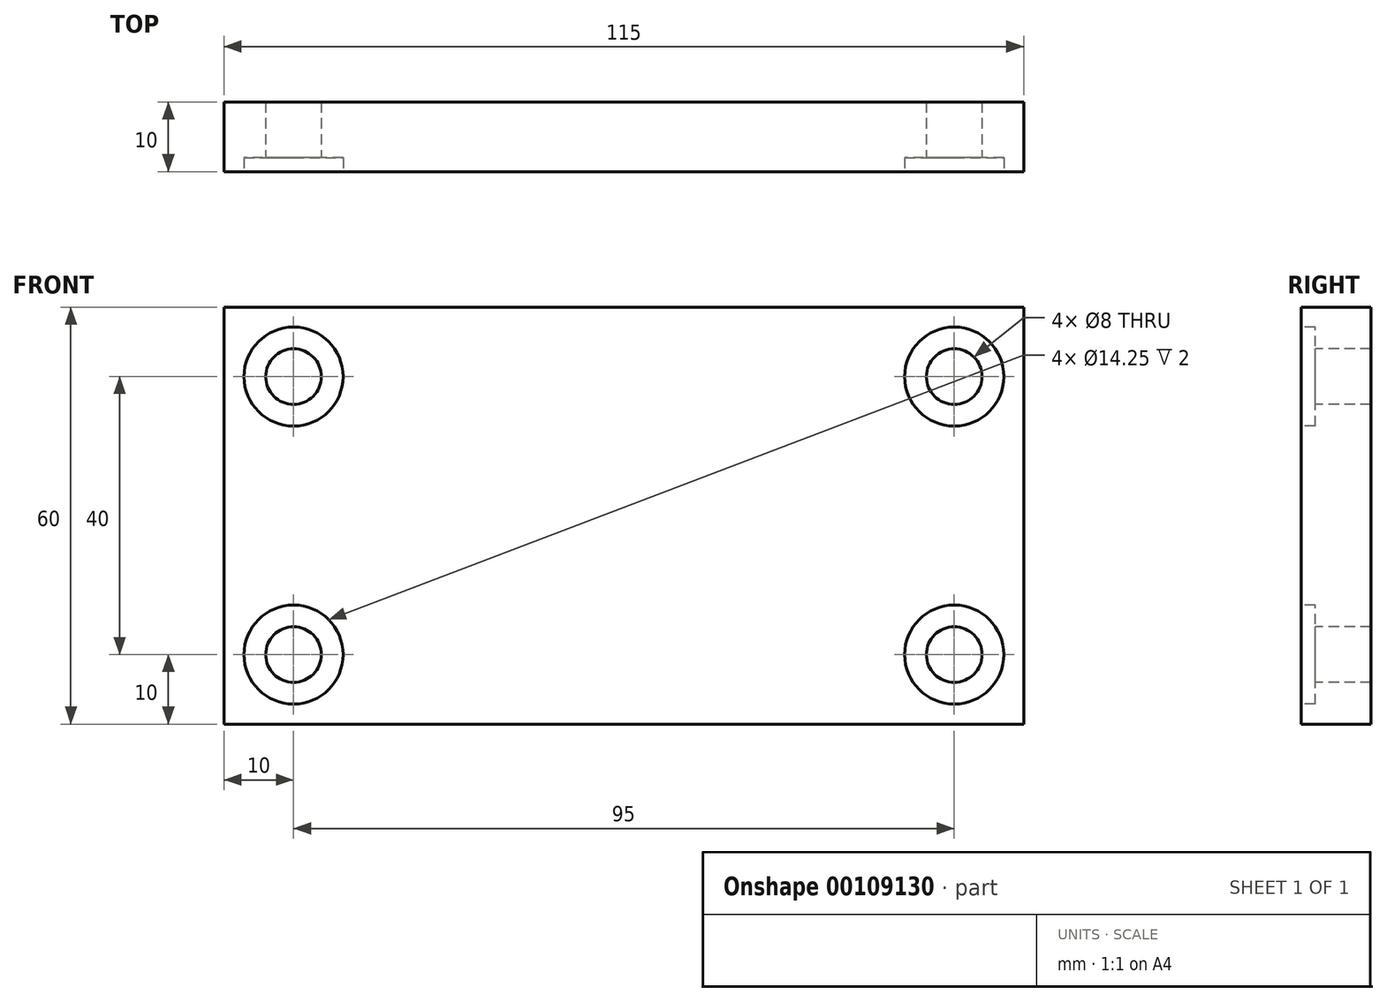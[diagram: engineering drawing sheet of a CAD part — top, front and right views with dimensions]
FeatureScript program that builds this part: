
annotation { "Feature Type Name" : "Feature", "Feature Type Description" : "" }
export const myFeature = defineFeature(function(context is Context, id is Id, definition is map)
    precondition{}
    {
        {
            var Q0;
            Q0=qCreatedBy(makeId("Front.planeOp"),FACE);
            var sketch = newSketch(context, id + "F0", { "sketchPlane" : qUnion([Q0])});
            skLineSegment(sketch, "E0.bottom", {"start": v(0, 0) * mm, "end": v(115, 0) * mm});
            skLineSegment(sketch, "E0.top", {"start": v(0, 60) * mm, "end": v(115, 60) * mm});
            skLineSegment(sketch, "E0.left", {"start": v(0, 0) * mm, "end": v(0, 60) * mm});
            skLineSegment(sketch, "E0.right", {"start": v(115, 0) * mm, "end": v(115, 60) * mm});
            skSolve(sketch);
        }
        {
            var Q0;
            Q0=makeQuery(id+"F0.imprint","IMPRINT",FACE,{"disambiguationData":[TD([[makeQuery(id+"F0.imprint","IMPRINT",EDGE,{"derivedFrom":sQuery(id+"F0.wireOp",EDGE,"E0.bottom")}),1.0]])]});
            extrude(context, id + "F1", {"entities" : qUnion([Q0]), "depth" : 10 * mm});
        }
        {
            var Q0;
            Q0=makeQuery(id+"F1.opExtrude","CAP_FACE",FACE,{"disambiguationData":[OSD([sQuery(id+"F0.wireOp",EDGE,"E0.bottom"),sQuery(id+"F0.wireOp",EDGE,"E0.top"),sQuery(id+"F0.wireOp",EDGE,"E0.left"),sQuery(id+"F0.wireOp",EDGE,"E0.right")])],"isStart":false});
            var sketch = newSketch(context, id + "F2", { "sketchPlane" : qUnion([Q0])});
            skLineSegment(sketch, "E1.bottom", {"start": v(0, 0) * mm, "end": v(10, 0) * mm});
            skLineSegment(sketch, "E1.left", {"start": v(0, 0) * mm, "end": v(0, 10) * mm});
            skLineSegment(sketch, "E2.left", {"start": v(10, 10) * mm, "end": v(10, 50) * mm});
            skLineSegment(sketch, "E2.right", {"start": v(105, 10) * mm, "end": v(105, 50) * mm});
            skPoint(sketch, "E3", {"position": v(10, 50) * mm});
            skPoint(sketch, "E4", {"position": v(105, 50) * mm});
            skPoint(sketch, "E5", {"position": v(105, 10) * mm});
            skPoint(sketch, "E6", {"position": v(10, 10) * mm});
            skSolve(sketch);
        }
        {
            var Q0;
            Q0=sQuery(id+"F2.wireOp",VERTEX,"E3");
            var Q1;
            Q1=sQuery(id+"F2.wireOp",VERTEX,"E4");
            var Q2;
            Q2=sQuery(id+"F2.wireOp",VERTEX,"E5");
            var Q3;
            Q3=sQuery(id+"F2.wireOp",VERTEX,"E6");
            var Q4;
            Q4=makeQuery(id+"F1.opExtrude","SWEPT_BODY",BODY,{"disambiguationData":[OSD([sQuery(id+"F0.wireOp",EDGE,"E0.bottom"),sQuery(id+"F0.wireOp",EDGE,"E0.top"),sQuery(id+"F0.wireOp",EDGE,"E0.left"),sQuery(id+"F0.wireOp",EDGE,"E0.right")])]});
            hole(context, id + "F3", {"style" : HoleStyle.C_BORE, "endStyle" : HoleEndStyle.BLIND, "holeDiameter" : 8 * mm, "cBoreDiameter" : 14.25 * mm, "cBoreDepth" : 2 * mm, "holeDepth" : 10 * mm, "locations" : qUnion([Q0, Q1, Q2, Q3]), "scope" : qUnion([Q4])});
        }
    });
